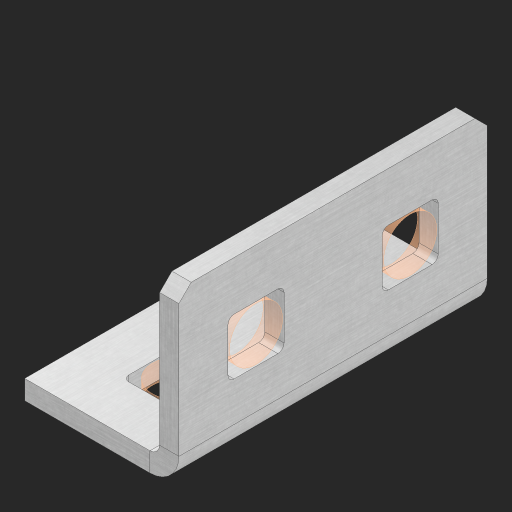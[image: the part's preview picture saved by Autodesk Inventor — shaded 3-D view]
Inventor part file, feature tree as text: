
AUTODESK INVENTOR PART (.ipt)
format: ipt  version: 2023 (Build 270158000, 158)  size: 401,920 bytes
history: native  units: in
note: dims shown in document units (in); Inventor stores cm internally (conversion verified against a paired STEP export)
features: sheet_metal_op x10, other x9, sketch x8, extrude x3, mirror x1, pattern_linear x1, chamfer x1
ambient origin geometry x8: Origin, YZ Plane, XZ Plane, XY Plane, X Axis, Y Axis, Z Axis, Center Point
bodies: Solid1 (feature_tree), Body (feature_tree)
feature tree (33):
  other  "Flange Pattern Plane"
  sheet_metal_op  "Flange Pattern"
  sheet_metal_op  "Body Pattern"
  other  "Arc Length"
  mirror  "Notch Mirror"
  pattern_linear  "Notch Pattern"  Spacing1=0.25in  [1 undecoded]
  chamfer  "End Chamfer"
  extrude  "Half Cut"  Depth=0.0625in
  sketch  "Sketch1"  dims[d0=1.5in]
  other  "Plate1"
  sketch  "Sketch2"  dims[d1=1.0in]
  other  "Plate2"
  sheet_metal_op  "Bend1"
  sheet_metal_op  "Corner1"
  sketch  "Sketch3"  dims[d2=0.0625in]
  other  "Flange Pattern Sketch"
  sketch  "Sketch7"  dims[d3=0.0625in]
  other  "Srf1"
  other  "Srf2"
  sketch  "Sketch8"  dims[d4=0.0312in]
  sketch  "Sketch9"  dims[d5=0.125in]
  other  "Srf91"
  sheet_metal_op  "Body Pattern Sketch"
  other  "Srf92"
  sketch  "Sketch13"  dims[d6=0.0625in]
  sketch  "Sketch14"  dims[d7=0.5in d8=90.0deg d9=0.0312in d10=0.25in d11=0.0625in d12=0.0625in d16=0.182in d17=0.02in d18=0.0625in d19=0.0in d20=0.25in d21=0.25in d46=0.172in d47=1.0in d48=0.0in d49=0.182in d50=0.02in d51=0.25in d52=0.25in d53=0.0625in d54=0.0in d55=0.172in d56=1.0in d57=0.0in d60=0.7874in d62=0.5in d63=0.3937in d65=0.5in d85=0.1473in d86=0.1782in d88=0.04in d89=0.0625in d90=0.0in d91=0.04in d92=0.0491in d95=2.5in d96=0.04in d97=0.25in d98=45.0deg d101=0.0in d102=2.497in d131=0.5in d132=0.7874in d134=0.5in d139=0.5in]
  sheet_metal_op  "Flange Stamp"
  sheet_metal_op  "Flange Circle"
  sheet_metal_op  "Body Stamp"
  sheet_metal_op  "Body Circle"
  sheet_metal_op  "Notch"
  extrude  "ExtrusionSrf2"  Depth=0.0625in
  extrude  "ExtrusionSrf92"  Depth=0.182in
note: 1 required parameter value undecoded (feature->parameter linkage not recoverable at this tier; creation-order binding heuristic only, values carry confidence <= 0.55)
